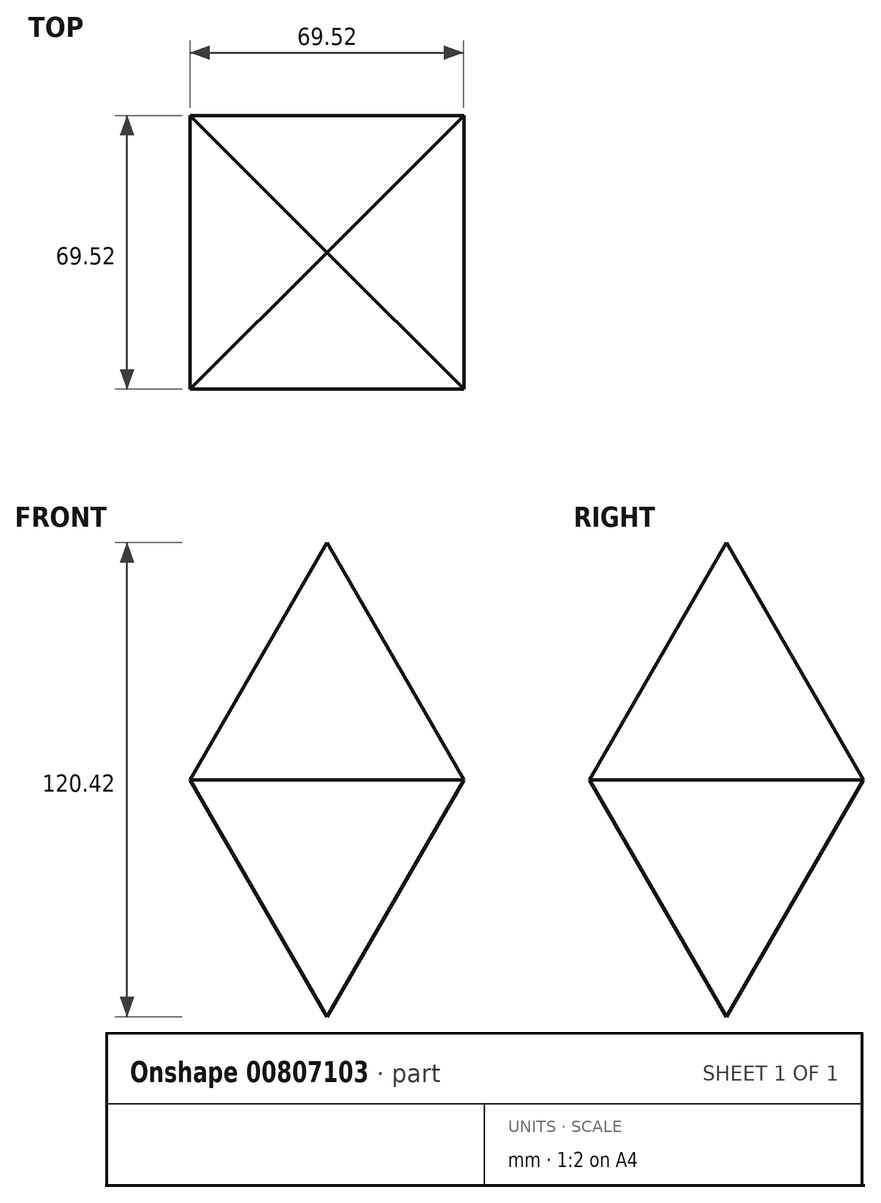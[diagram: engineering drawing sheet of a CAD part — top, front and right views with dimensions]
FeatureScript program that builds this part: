
annotation { "Feature Type Name" : "Feature", "Feature Type Description" : "" }
export const myFeature = defineFeature(function(context is Context, id is Id, definition is map)
    precondition{}
    {
        {
            var Q0;
            Q0=qCreatedBy(makeId("Top.planeOp"),FACE);
            var sketch = newSketch(context, id + "F0", { "sketchPlane" : qUnion([Q0])});
            skLineSegment(sketch, "E0.bottom", {"start": v(34.76, 34.76) * mm, "end": v(-34.76, 34.76) * mm});
            skLineSegment(sketch, "E0.top", {"start": v(34.76, -34.76) * mm, "end": v(-34.76, -34.76) * mm});
            skLineSegment(sketch, "E0.left", {"start": v(34.76, 34.76) * mm, "end": v(34.76, -34.76) * mm});
            skLineSegment(sketch, "E0.right", {"start": v(-34.76, 34.76) * mm, "end": v(-34.76, -34.76) * mm});
            skPoint(sketch, "E0.middle", {"position": v(0, 0) * mm});
            skSolve(sketch);
        }
        {
            var Q0;
            Q0 = qSketchRegion(id + "F0", true);
            extrude(context, id + "F1", {"entities" : qUnion([Q0]), "depth" : 89.66 * mm, "offsetDistance" : 25.4 * mm, "hasDraft" : true, "draftAngle" : 30 * degree, "draftPullDirection" : true, "hasSecondDirection" : true, "secondDirectionOppositeDirection" : true, "secondDirectionDepth" : 65.28 * mm, "hasSecondDirectionDraft" : true, "secondDirectionDraftAngle" : 30 * degree, "secondDirectionDraftPullDirection" : true});
        }
    });
